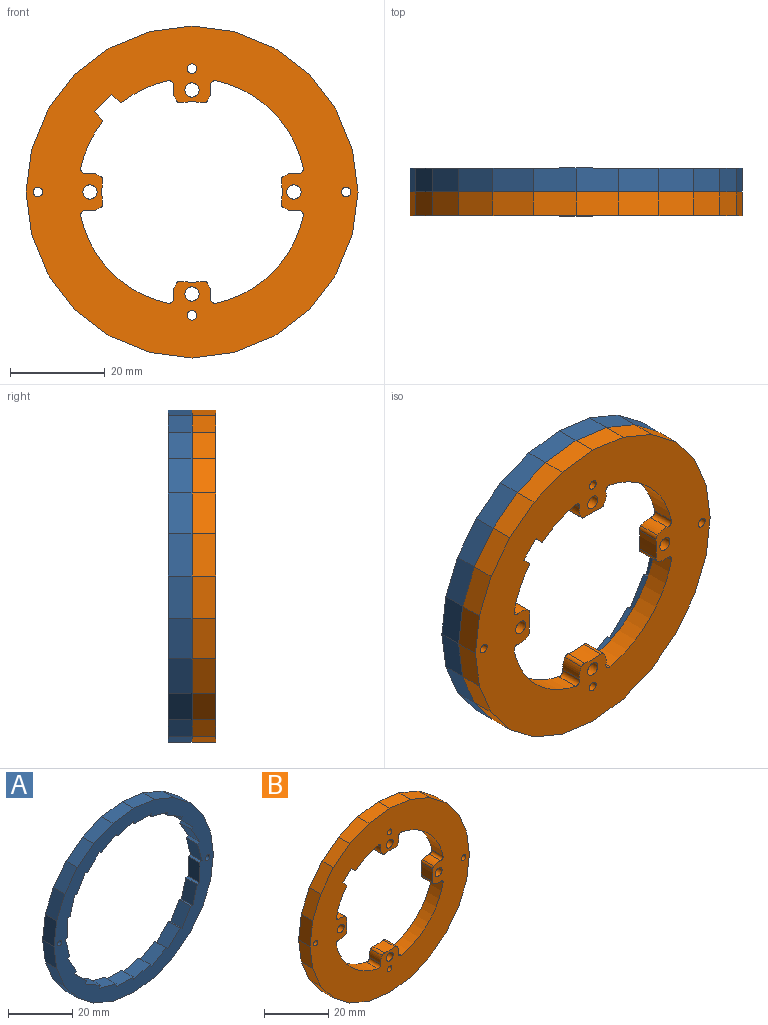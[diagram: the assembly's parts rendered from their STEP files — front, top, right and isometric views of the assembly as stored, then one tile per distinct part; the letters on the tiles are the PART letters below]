
ASSEMBLY  parts=2 mates=1
PART A: 76 faces, bbox 70x5x70 mm
  f0: plane 5x1.04mm, normal (-1,0,0), area 5.2mm2, adj f1,f73,f74,f75
  f1: plane 7.24x5mm, normal (-0.26,0,-0.97), area 37.5mm2, adj f0,f2,f74,f75
  f2: plane 5x1mm, normal (-0.97,0,0.26), area 5.2mm2, adj f1,f3,f74,f75
  f3: plane 6.5x5mm, normal (-0.5,0,-0.87), area 37.5mm2, adj f2,f4,f74,f75
  f4: plane 5x0.92mm, normal (-0.87,0,0.5), area 5.3mm2, adj f3,f5,f74,f75
  f5: plane 5.3x5.3mm, normal (-0.71,0,-0.71), area 37.5mm2, adj f4,f6,f74,f75
  f6: plane 5x0.75mm, normal (-0.71,0,0.71), area 5.3mm2, adj f5,f7,f74,f75
  f7: plane 6.5x5mm, normal (-0.87,0,-0.5), area 37.5mm2, adj f6,f8,f74,f75
  f8: plane 5x0.9mm, normal (-0.5,0,0.87), area 5.2mm2, adj f7,f9,f74,f75
  f9: plane 7.25x5mm, normal (-0.97,0,-0.26), area 37.5mm2, adj f8,f10,f74,f75
  f10: plane 5x1mm, normal (-0.26,0,0.97), area 5.2mm2, adj f9,f11,f74,f75
  f11: plane 7.5x5mm, normal (-1,0,0), area 37.5mm2, adj f10,f12,f74,f75
  f12: plane 5x1.08mm, normal (-0.13,0,0.99), area 5.4mm2, adj f11,f13,f74,f75
  f13: plane 7.09x5mm, normal (-0.97,0,0.26), area 36.7mm2, adj f12,f14,f74,f75
  f14: plane 5x1mm, normal (0.26,0,0.97), area 5.2mm2, adj f13,f15,f74,f75
  f15: plane 6.48x5mm, normal (-0.86,0,0.5), area 37.5mm2, adj f14,f16,f74,f75
  f16: plane 5x0.9mm, normal (0.5,0,0.86), area 5.2mm2, adj f15,f17,f74,f75
  f17: plane 5.32x5.29mm, normal (-0.71,0,0.71), area 37.5mm2, adj f16,f18,f74,f75
  f18: plane 5x0.73mm, normal (0.71,0,0.71), area 5.2mm2, adj f17,f19,f74,f75
  f19: plane 6.51x5mm, normal (-0.5,0,0.87), area 37.5mm2, adj f18,f20,f74,f75
  f20: plane 5x0.9mm, normal (0.87,0,0.5), area 5.2mm2, adj f19,f21,f74,f75
  f21: plane 7.25x5mm, normal (-0.26,0,0.97), area 37.5mm2, adj f20,f22,f74,f75
  f22: plane 5x1mm, normal (0.97,0,0.26), area 5.2mm2, adj f21,f23,f74,f75
  f23: plane 7.5x5mm, normal (0,0,1), area 37.5mm2, adj f22,f24,f74,f75
  f24: plane 5x1.04mm, normal (1,0,0), area 5.2mm2, adj f23,f25,f74,f75
  f25: plane 7.24x5mm, normal (0.26,0,0.97), area 37.5mm2, adj f24,f26,f74,f75
  f26: plane 5x1mm, normal (0.97,0,-0.26), area 5.2mm2, adj f25,f27,f74,f75
  f27: plane 6.48x5mm, normal (0.5,0,0.86), area 37.5mm2, adj f26,f28,f74,f75
  f28: plane 5x0.9mm, normal (0.86,0,-0.5), area 5.2mm2, adj f27,f29,f74,f75
  f29: plane 5.32x5.29mm, normal (0.71,0,0.71), area 37.5mm2, adj f28,f30,f74,f75
  f30: plane 5x0.73mm, normal (0.71,0,-0.71), area 5.2mm2, adj f29,f31,f74,f75
  f31: plane 6.51x5mm, normal (0.87,0,0.5), area 37.5mm2, adj f30,f32,f74,f75
  f32: plane 5x0.9mm, normal (0.5,0,-0.87), area 5.2mm2, adj f31,f33,f74,f75
  f33: plane 7.25x5mm, normal (0.97,0,0.26), area 37.5mm2, adj f32,f34,f74,f75
  f34: plane 5x1mm, normal (0.26,0,-0.97), area 5.2mm2, adj f33,f35,f74,f75
  f35: plane 7.5x5mm, normal (1,0,0), area 37.5mm2, adj f34,f36,f74,f75
  f36: plane 5x1.04mm, normal (0,0,-1), area 5.2mm2, adj f35,f37,f74,f75
  f37: plane 7.24x5mm, normal (0.97,0,-0.26), area 37.5mm2, adj f36,f38,f74,f75
  f38: plane 5x1mm, normal (-0.26,0,-0.97), area 5.2mm2, adj f37,f39,f74,f75
  f39: plane 6.48x5mm, normal (0.86,0,-0.5), area 37.5mm2, adj f38,f40,f74,f75
  f40: plane 5x0.9mm, normal (-0.5,0,-0.86), area 5.2mm2, adj f39,f41,f74,f75
  f41: plane 5.32x5.29mm, normal (0.71,0,-0.71), area 37.5mm2, adj f40,f42,f74,f75
  f42: plane 5x0.73mm, normal (-0.71,0,-0.71), area 5.2mm2, adj f41,f43,f74,f75
  f43: plane 6.51x5mm, normal (0.5,0,-0.87), area 37.5mm2, adj f42,f44,f74,f75
  f44: plane 5x0.9mm, normal (-0.87,0,-0.5), area 5.2mm2, adj f43,f45,f74,f75
  f45: plane 7.25x5mm, normal (0.26,0,-0.97), area 37.5mm2, adj f44,f46,f74,f75
  f46: plane 5x1mm, normal (-0.97,0,-0.26), area 5.2mm2, adj f45,f73,f74,f75
  f47: plane 9.06x5mm, normal (0.13,0,0.99), area 45.7mm2, adj f48,f70,f74,f75
  f48: plane 9.06x5mm, normal (-0.13,0,0.99), area 45.7mm2, adj f47,f49,f74,f75
  f49: plane 8.44x5mm, normal (-0.38,0,0.92), area 45.7mm2, adj f48,f50,f74,f75
  f50: plane 7.25x5.56mm, normal (-0.61,0,0.79), area 45.7mm2, adj f49,f51,f74,f75
  f51: plane 7.25x5.56mm, normal (-0.79,0,0.61), area 45.7mm2, adj f50,f52,f74,f75
  f52: plane 8.44x5mm, normal (-0.92,0,0.38), area 45.7mm2, adj f51,f53,f74,f75
  f53: plane 9.06x5mm, normal (-0.99,0,0.13), area 45.7mm2, adj f52,f54,f74,f75
  f54: plane 9.06x5mm, normal (-0.99,0,-0.13), area 45.7mm2, adj f53,f55,f74,f75
  f55: plane 8.44x5mm, normal (-0.92,0,-0.38), area 45.7mm2, adj f54,f56,f74,f75
  f56: plane 7.25x5.56mm, normal (-0.79,0,-0.61), area 45.7mm2, adj f55,f57,f74,f75
  f57: plane 7.25x5.56mm, normal (-0.61,0,-0.79), area 45.7mm2, adj f56,f58,f74,f75
  f58: plane 8.44x5mm, normal (-0.38,0,-0.92), area 45.7mm2, adj f57,f59,f74,f75
  f59: plane 9.06x5mm, normal (-0.13,0,-0.99), area 45.7mm2, adj f58,f60,f74,f75
  f60: plane 9.06x5mm, normal (0.13,0,-0.99), area 45.7mm2, adj f59,f61,f74,f75
  f61: plane 8.44x5mm, normal (0.38,0,-0.92), area 45.7mm2, adj f60,f62,f74,f75
  f62: plane 7.25x5.56mm, normal (0.61,0,-0.79), area 45.7mm2, adj f61,f63,f74,f75
  f63: plane 7.25x5.56mm, normal (0.79,0,-0.61), area 45.7mm2, adj f62,f64,f74,f75
  f64: plane 8.44x5mm, normal (0.92,0,-0.38), area 45.7mm2, adj f63,f65,f74,f75
  f65: plane 9.06x5mm, normal (0.99,0,-0.13), area 45.7mm2, adj f64,f66,f74,f75
  f66: plane 9.06x5mm, normal (0.99,0,0.13), area 45.7mm2, adj f65,f67,f74,f75
  f67: plane 8.44x5mm, normal (0.92,0,0.38), area 45.7mm2, adj f66,f68,f74,f75
  f68: plane 7.25x5.56mm, normal (0.79,0,0.61), area 45.7mm2, adj f67,f69,f74,f75
  f69: plane 7.25x5.56mm, normal (0.61,0,0.79), area 45.7mm2, adj f68,f70,f74,f75
  f70: plane 8.44x5mm, normal (0.38,0,0.92), area 45.7mm2, adj f47,f69,f74,f75
  f71: cylinder r=1mm len=5mm, axis (0,1,0), area 31.4mm2, adj f74,f75
  f72: cylinder r=1mm len=5mm, axis (0,1,0), area 31.4mm2, adj f74,f75
  f73: plane 7.5x5mm, normal (0,0,-1), area 37.5mm2, adj f0,f46,f74,f75
  f74: plane 70x70mm, normal (0,-1,0), area 1092.9mm2, adj f0,f1,f2,f3,f4,f5,f6,f7
  f75: plane 70x70mm, normal (0,1,0), area 1092.9mm2, adj f0,f1,f2,f3,f4,f5,f6,f7
PART B: 72 faces, bbox 70x5x70 mm
  f0: plane 9.06x5mm, normal (0.13,0,0.99), area 45.7mm2, adj f1,f69,f70,f71
  f1: plane 9.06x5mm, normal (-0.13,0,0.99), area 45.7mm2, adj f0,f2,f70,f71
  f2: plane 8.44x5mm, normal (-0.38,0,0.92), area 45.7mm2, adj f1,f3,f70,f71
  f3: plane 7.25x5.56mm, normal (-0.61,0,0.79), area 45.7mm2, adj f2,f4,f70,f71
  f4: plane 7.25x5.56mm, normal (-0.79,0,0.61), area 45.7mm2, adj f3,f5,f70,f71
  f5: plane 8.44x5mm, normal (-0.92,0,0.38), area 45.7mm2, adj f4,f6,f70,f71
  f6: plane 9.06x5mm, normal (-0.99,0,0.13), area 45.7mm2, adj f5,f7,f70,f71
  f7: plane 9.06x5mm, normal (-0.99,0,-0.13), area 45.7mm2, adj f6,f8,f70,f71
  f8: plane 8.44x5mm, normal (-0.92,0,-0.38), area 45.7mm2, adj f7,f9,f70,f71
  f9: plane 7.25x5.56mm, normal (-0.79,0,-0.61), area 45.7mm2, adj f8,f10,f70,f71
  f10: plane 7.25x5.56mm, normal (-0.61,0,-0.79), area 45.7mm2, adj f9,f11,f70,f71
  f11: plane 8.44x5mm, normal (-0.38,0,-0.92), area 45.7mm2, adj f10,f12,f70,f71
  f12: plane 9.06x5mm, normal (-0.13,0,-0.99), area 45.7mm2, adj f11,f13,f70,f71
  f13: plane 9.06x5mm, normal (0.13,0,-0.99), area 45.7mm2, adj f12,f14,f70,f71
  f14: plane 8.44x5mm, normal (0.38,0,-0.92), area 45.7mm2, adj f13,f15,f70,f71
  f15: plane 7.25x5.56mm, normal (0.61,0,-0.79), area 45.7mm2, adj f14,f16,f70,f71
  f16: plane 7.25x5.56mm, normal (0.79,0,-0.61), area 45.7mm2, adj f15,f17,f70,f71
  f17: plane 8.44x5mm, normal (0.92,0,-0.38), area 45.7mm2, adj f16,f18,f70,f71
  f18: plane 9.06x5mm, normal (0.99,0,-0.13), area 45.7mm2, adj f17,f19,f70,f71
  f19: plane 9.06x5mm, normal (0.99,0,0.13), area 45.7mm2, adj f18,f20,f70,f71
  f20: plane 8.44x5mm, normal (0.92,0,0.38), area 45.7mm2, adj f19,f21,f70,f71
  f21: plane 7.25x5.56mm, normal (0.79,0,0.61), area 45.7mm2, adj f20,f22,f70,f71
  f22: plane 7.25x5.56mm, normal (0.61,0,0.79), area 45.7mm2, adj f21,f69,f70,f71
  f23: cylinder r=1mm len=5mm, axis (0,1,0), area 9.9mm2, adj f24,f60,f70,f71
  f24: cylinder r=24mm len=18.33mm, axis (0,1,0), area 136.9mm2, adj f23,f25,f70,f71
  f25: cylinder r=1mm len=5mm, axis (0,1,0), area 9.9mm2, adj f24,f26,f70,f71
  f26: cylinder r=4mm len=5mm, axis (0,1,0), area 15.6mm2, adj f25,f27,f70,f71
  f27: cylinder r=1mm len=5mm, axis (0,1,0), area 5.6mm2, adj f26,f28,f70,f71
  f28: cylinder r=19mm len=5mm, axis (0,1,0), area 23.8mm2, adj f27,f29,f70,f71
  f29: cylinder r=1mm len=5mm, axis (0,1,0), area 5.6mm2, adj f28,f30,f70,f71
  f30: cylinder r=4mm len=5mm, axis (0,1,0), area 15.6mm2, adj f29,f31,f70,f71
  f31: cylinder r=1mm len=5mm, axis (0,1,0), area 9.9mm2, adj f30,f32,f70,f71
  f32: cylinder r=24mm len=18.33mm, axis (0,1,0), area 136.9mm2, adj f31,f33,f70,f71
  f33: cylinder r=1mm len=5mm, axis (0,1,0), area 9.9mm2, adj f32,f34,f70,f71
  f34: cylinder r=4mm len=5mm, axis (0,1,0), area 15.6mm2, adj f33,f35,f70,f71
  f35: cylinder r=1mm len=5mm, axis (0,1,0), area 5.6mm2, adj f34,f36,f70,f71
  f36: cylinder r=19mm len=5mm, axis (0,1,0), area 23.8mm2, adj f35,f37,f70,f71
  f37: cylinder r=1mm len=5mm, axis (0,1,0), area 5.6mm2, adj f36,f38,f70,f71
  f38: cylinder r=4mm len=5mm, axis (0,1,0), area 15.6mm2, adj f37,f39,f70,f71
  f39: cylinder r=1mm len=5mm, axis (0,1,0), area 9.9mm2, adj f38,f40,f70,f71
  f40: cylinder r=24mm len=9.78mm, axis (0,1,0), area 54.5mm2, adj f39,f41,f70,f71
  f41: cylinder r=0.2mm len=5mm, axis (0,1,0), area 1.5mm2, adj f40,f42,f70,f71
  f42: plane 5x1.74mm, normal (0.71,0,0.71), area 12.3mm2, adj f41,f43,f70,f71
  f43: plane 5x3.68mm, normal (0.71,0,-0.71), area 26mm2, adj f42,f44,f70,f71
  f44: plane 5x1.74mm, normal (-0.71,0,-0.71), area 12.3mm2, adj f43,f45,f70,f71
  f45: cylinder r=0.2mm len=5mm, axis (0,1,0), area 1.5mm2, adj f44,f46,f70,f71
  f46: cylinder r=24mm len=9.78mm, axis (0,1,0), area 54.5mm2, adj f45,f47,f70,f71
  f47: cylinder r=1mm len=5mm, axis (0,1,0), area 9.9mm2, adj f46,f48,f70,f71
  f48: cylinder r=4mm len=5mm, axis (0,1,0), area 15.6mm2, adj f47,f49,f70,f71
  f49: cylinder r=1mm len=5mm, axis (0,1,0), area 5.6mm2, adj f48,f50,f70,f71
  f50: cylinder r=19mm len=5mm, axis (0,1,0), area 23.8mm2, adj f49,f51,f70,f71
  f51: cylinder r=1mm len=5mm, axis (0,1,0), area 5.6mm2, adj f50,f52,f70,f71
  f52: cylinder r=4mm len=5mm, axis (0,1,0), area 15.6mm2, adj f51,f53,f70,f71
  f53: cylinder r=1mm len=5mm, axis (0,1,0), area 9.9mm2, adj f52,f54,f70,f71
  f54: cylinder r=24mm len=18.33mm, axis (0,1,0), area 136.9mm2, adj f53,f55,f70,f71
  f55: cylinder r=1mm len=5mm, axis (0,1,0), area 9.9mm2, adj f54,f56,f70,f71
  f56: cylinder r=4mm len=5mm, axis (0,1,0), area 15.6mm2, adj f55,f57,f70,f71
  f57: cylinder r=1mm len=5mm, axis (0,1,0), area 5.6mm2, adj f56,f58,f70,f71
  f58: cylinder r=19mm len=5mm, axis (0,1,0), area 23.8mm2, adj f57,f59,f70,f71
  f59: cylinder r=1mm len=5mm, axis (0,1,0), area 5.6mm2, adj f58,f60,f70,f71
  f60: cylinder r=4mm len=5mm, axis (0,1,0), area 15.6mm2, adj f23,f59,f70,f71
  f61: cylinder r=1mm len=5mm, axis (0,1,0), area 31.4mm2, adj f70,f71
  f62: cylinder r=1mm len=5mm, axis (0,1,0), area 31.4mm2, adj f70,f71
  f63: cylinder r=1.5mm len=5mm, axis (0,1,0), area 47.1mm2, adj f70,f71
  f64: cylinder r=1.5mm len=5mm, axis (0,1,0), area 47.1mm2, adj f70,f71
  f65: cylinder r=1.5mm len=5mm, axis (0,1,0), area 47.1mm2, adj f70,f71
  f66: cylinder r=1.5mm len=5mm, axis (0,1,0), area 47.1mm2, adj f70,f71
  f67: cylinder r=1mm len=5mm, axis (0,1,0), area 31.4mm2, adj f70,f71
  f68: cylinder r=1mm len=5mm, axis (0,1,0), area 31.4mm2, adj f70,f71
  f69: plane 8.44x5mm, normal (0.38,0,0.92), area 45.7mm2, adj f0,f22,f70,f71
  f70: plane 70x70mm, normal (0,-1,0), area 2094.8mm2, adj f0,f1,f2,f3,f4,f5,f6,f7
  f71: plane 70x70mm, normal (0,1,0), area 2094.8mm2, adj f0,f1,f2,f3,f4,f5,f6,f7
PLACE A t=(-28.09,29.05,-30.64)mm
PLACE B t=(-28.09,24.05,-30.64)mm
MATE fastened B.f62 <-> A.f72  axis (0,1,0) through (4.41,24.05,-30.64)mm
